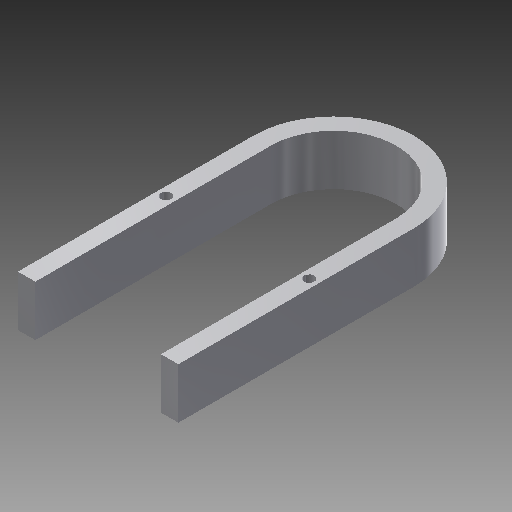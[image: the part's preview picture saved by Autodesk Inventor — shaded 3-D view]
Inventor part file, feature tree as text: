
AUTODESK INVENTOR PART (.ipt)
format: ipt  version: 2018 (Build 220112000, 112)  size: 119,296 bytes
history: native  units: mm
features: extrude x1, hole x1, mirror x1
ambient origin geometry x8: Origin, YZ Plane, XZ Plane, XY Plane, X Axis, Y Axis, Z Axis, Center Point
bodies: Volumenkörper1 (feature_tree)
feature tree (3):
  extrude  "Extrusion1"  Depth=67.5mm
  hole  "Bohrung1"  [1 undecoded]
  mirror  "Spiegeln2"
note: 1 required parameter value undecoded (feature->parameter linkage not recoverable at this tier; creation-order binding heuristic only, values carry confidence <= 0.55)
